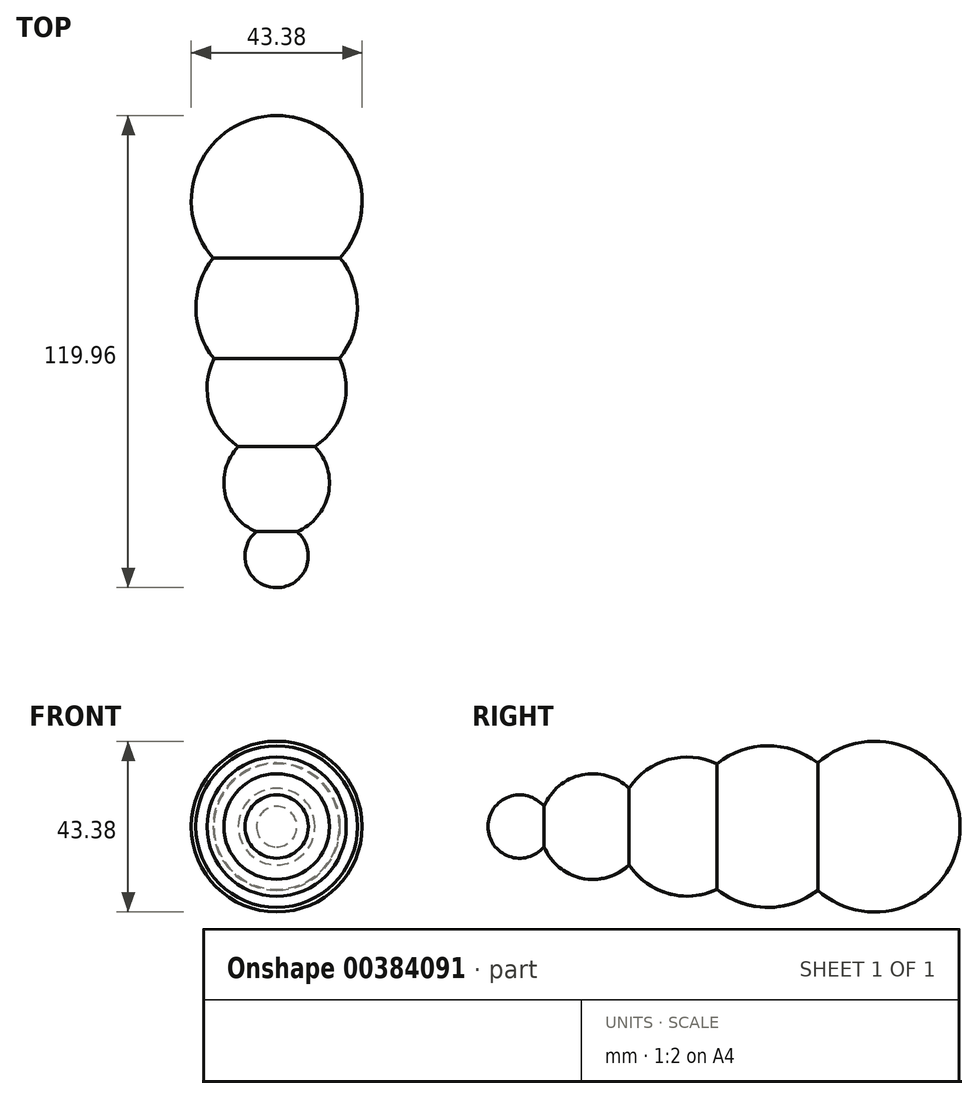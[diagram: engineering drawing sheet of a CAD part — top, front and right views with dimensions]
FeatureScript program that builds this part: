
annotation { "Feature Type Name" : "Feature", "Feature Type Description" : "" }
export const myFeature = defineFeature(function(context is Context, id is Id, definition is map)
    precondition{}
    {
        {
            var Q0;
            Q0=qCreatedBy(makeId("Top.planeOp"),FACE);
            var sketch = newSketch(context, id + "F0", { "sketchPlane" : qUnion([Q0])});
            skArc(sketch, "E0", {"start": v(16.16, 25.3) * mm, "mid": v(19.8, 48.63) * mm, "end": v(0, 61.47) * mm});
            skArc(sketch, "E1", {"start": v(0, -58.5) * mm, "mid": v(7.57, -53.17) * mm, "end": v(5.13, -44.25) * mm});
            skArc(sketch, "E2.trimOffspring", {"start": v(15.95, -0.28) * mm, "mid": v(20.53, 12.48) * mm, "end": v(16.16, 25.3) * mm});
            skArc(sketch, "E3.trimOffspring", {"start": v(9.74, -22.63) * mm, "mid": v(17.03, -12.61) * mm, "end": v(15.95, -0.28) * mm});
            skArc(sketch, "E4.trimOffspring", {"start": v(5.13, -44.25) * mm, "mid": v(13.12, -34.65) * mm, "end": v(9.74, -22.63) * mm});
            skPoint(sketch, "E5.startSnap0", {"position": v(0, 61.47) * mm});
            skPoint(sketch, "E5.endSnap0", {"position": v(0, -58.5) * mm});
            skPoint(sketch, "E6.orphan", {"position": v(0, 44.04) * mm});
            skLineSegment(sketch, "E7", {"start": v(0, 68.33) * mm, "end": v(0, -71.26) * mm});
            skSolve(sketch);
        }
        {
            var Q0;
            Q0=sQuery(id+"F0.wireOp",EDGE,"E2.trimOffspring");
            var Q1;
            Q1=sQuery(id+"F0.wireOp",EDGE,"E4.trimOffspring");
            var Q2;
            Q2=sQuery(id+"F0.wireOp",EDGE,"E0");
            var Q3;
            Q3=sQuery(id+"F0.wireOp",EDGE,"E1");
            var Q4;
            Q4=sQuery(id+"F0.wireOp",EDGE,"E3.trimOffspring");
            var Q5;
            Q5=sQuery(id+"F0.wireOp",EDGE,"E7");
            revolve(context, id + "F1", {"bodyType" : ToolBodyType.SURFACE, "surfaceEntities" : qUnion([Q0, Q1, Q2, Q3, Q4]), "axis" : qUnion([Q5]), "revolveType" : RevolveType.FULL});
        }
    });
